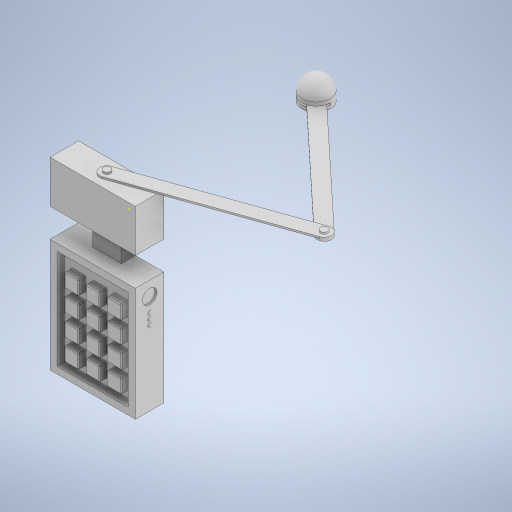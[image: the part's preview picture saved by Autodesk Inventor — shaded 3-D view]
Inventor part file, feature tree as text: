
AUTODESK INVENTOR PART (.ipt)
format: ipt  version: 2024 (Build 280153000, 153)  size: 624,640 bytes
history: native  units: in
note: dims shown in document units (in); Inventor stores cm internally (conversion verified against a paired STEP export)
features: sketch x14, extrude x13, fillet x5
ambient origin geometry x8: Origin, YZ Plane, XZ Plane, XY Plane, X Axis, Y Axis, Z Axis, Center Point
bodies: Body1 (feature_tree)
feature tree (32):
  extrude  "Extrusion2"  Depth=1.0in TaperAngle=0.0deg
  fillet  "Fillet1"  Radius=1.0in
  extrude  "Extrusion3"  Depth=0.25in
  extrude  "Extrusion5"  Depth=12.0in
  extrude  "Extrusion6"  Depth=0.125in TaperAngle=0.0deg
  extrude  "Extrusion7"  Depth=1.0in
  extrude  "Extrusion8"  Depth=0.5in
  extrude  "Extrusion9"  Depth=0.5in
  extrude  "Extrusion10"  Depth=6.0in
  extrude  "Extrusion11"  Depth=3.0in TaperAngle=0.0deg
  sketch  "Sketch13"  dims[d41=2.0in d42=1.0in]
  extrude  "Extrusion12"  Depth=1.0in
  extrude  "Extrusion13"  Depth=1.0in
  extrude  "Extrusion14"  Depth=8.0in TaperAngle=0.0deg
  extrude  "Extrusion15"  Depth=7.0in
  fillet  "Fillet3"  Radius=4.0in
  fillet  "Fillet4"  Radius=3.0in
  fillet  "Fillet5"  Radius=0.5in
  fillet  "Fillet6"  Radius=0.5in
  sketch  "Sketch2"  dims[d4=2.0in d5=1.625in d6=0.0in d7=1.0in]
  sketch  "Sketch3"  dims[d8=0.125in d9=0.25in]
  sketch  "Sketch5"  dims[d10=5.0in d11=0.0in d16=12.0in]
  sketch  "Sketch6"  dims[d17=1.0in d18=0.125in d19=0.0in]
  sketch  "Sketch7"  dims[d20=12.0in d21=1.0in]
  sketch  "Sketch8"  dims[d22=0.125in d23=0.0in d24=0.5in]
  sketch  "Sketch9"  dims[d25=0.125in d26=0.875in d27=0.0in d28=0.0in d29=0.5in]
  sketch  "Sketch11"  dims[d30=0.125in d31=0.375in d32=0.0in d33=0.0in d34=6.0in]
  sketch  "Sketch12"  dims[d35=2.0in d36=3.0in d37=0.0in]
  sketch  "Sketch14"  dims[d45=2.0in d46=1.0in]
  sketch  "Sketch15"  dims[d47=2.0in d48=0.0in d49=8.0in d50=0.0in]
  sketch  "Sketch16"  dims[d51=5.0in d52=7.0in d53=4.0in d54=3.0in d55=0.5in d56=0.0in d57=0.5in]
  sketch  "Sketch17"  dims[d58=0.5in d59=1.0in d60=1.0in d61=1.1811in d63=1.5in d64=1.5748in d66=1.5in d69=0.5in d70=0.0in d71=1.0in d72=0.25in d73=1.0in d75=1.0in d77=1.1811in d79=0.375in d80=0.3937in d82=1.0in d84=0.125in d85=0.0in d86=0.25in d87=2.0in d88=1.0in d89=1.1811in d91=0.375in d92=0.3937in d94=1.0in d96=0.125in d97=0.0in d98=0.125in d99=0.0625in d100=0.0625in d101=0.0625in d39=0.5in d40=0.0344in]
